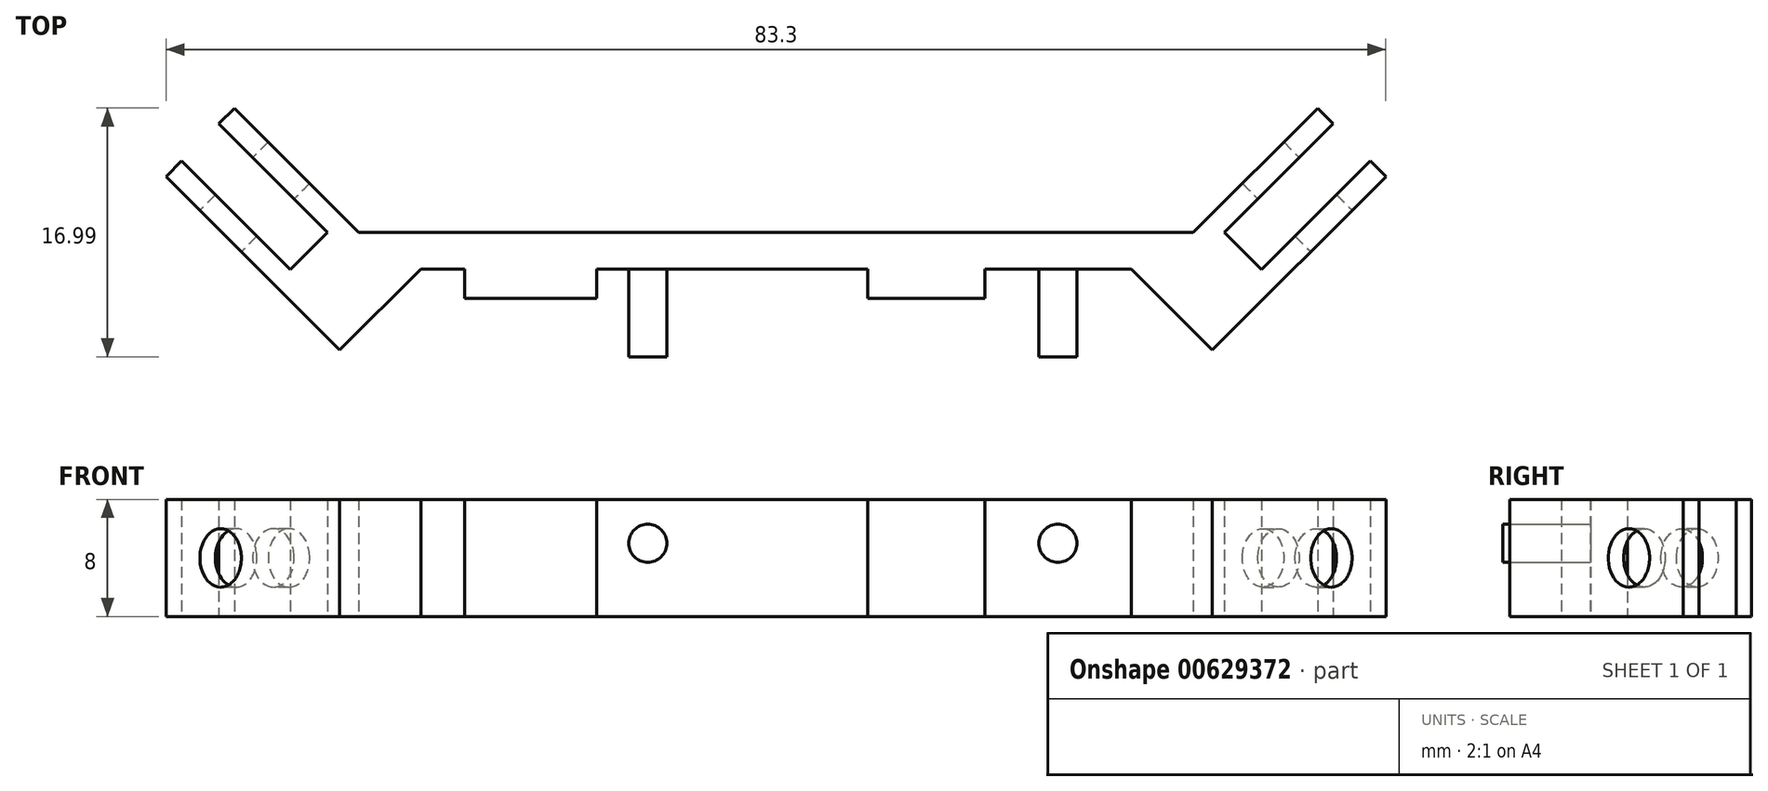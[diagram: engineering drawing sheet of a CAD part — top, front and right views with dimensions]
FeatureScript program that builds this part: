
annotation { "Feature Type Name" : "Feature", "Feature Type Description" : "" }
export const myFeature = defineFeature(function(context is Context, id is Id, definition is map)
    precondition{}
    {
        {
            var Q0;
            Q0=qCreatedBy(makeId("Top.planeOp"),FACE);
            var sketch = newSketch(context, id + "F0", { "sketchPlane" : qUnion([Q0])});
            skLineSegment(sketch, "E0.bottom", {"start": v(-28.5, -30) * mm, "end": v(28.5, -30) * mm});
            skPoint(sketch, "E0.middle", {"position": v(0, 0) * mm});
            skLineSegment(sketch, "E1", {"start": v(30.62, -30) * mm, "end": v(38.05, -22.58) * mm});
            skLineSegment(sketch, "E2.0", {"start": v(33.17, -32.55) * mm, "end": v(40.6, -25.12) * mm});
            skLineSegment(sketch, "E3.0", {"start": v(28.5, -30) * mm, "end": v(36.99, -21.51) * mm});
            skLineSegment(sketch, "E4", {"start": v(30.62, -30) * mm, "end": v(33.17, -32.55) * mm});
            skLineSegment(sketch, "E5.0", {"start": v(29.8, -38.04) * mm, "end": v(41.65, -26.18) * mm});
            skLineSegment(sketch, "E6", {"start": v(36.99, -21.51) * mm, "end": v(38.05, -22.58) * mm});
            skLineSegment(sketch, "E7.0", {"start": v(-24.26, -32.5) * mm, "end": v(24.26, -32.5) * mm});
            skLineSegment(sketch, "E8", {"start": v(24.26, -32.5) * mm, "end": v(29.8, -38.04) * mm});
            skLineSegment(sketch, "E9.trimOffspring", {"start": v(40.6, -25.12) * mm, "end": v(41.65, -26.18) * mm});
            skLineSegment(sketch, "E10.MirrorCS", {"start": v(-24.26, -32.5) * mm, "end": v(-29.8, -38.04) * mm});
            skLineSegment(sketch, "E11.MirrorCS", {"start": v(-29.8, -38.04) * mm, "end": v(-41.65, -26.18) * mm});
            skLineSegment(sketch, "E12.MirrorCS", {"start": v(-40.6, -25.12) * mm, "end": v(-41.65, -26.18) * mm});
            skLineSegment(sketch, "E13.MirrorCS", {"start": v(-33.17, -32.55) * mm, "end": v(-40.6, -25.12) * mm});
            skLineSegment(sketch, "E14.MirrorCS", {"start": v(-30.62, -30) * mm, "end": v(-33.17, -32.55) * mm});
            skLineSegment(sketch, "E15.MirrorCS", {"start": v(-30.62, -30) * mm, "end": v(-38.05, -22.58) * mm});
            skLineSegment(sketch, "E16.MirrorCS", {"start": v(-36.99, -21.51) * mm, "end": v(-38.05, -22.58) * mm});
            skLineSegment(sketch, "E17.MirrorCS", {"start": v(-28.5, -30) * mm, "end": v(-36.99, -21.51) * mm});
            skSolve(sketch);
        }
        {
            var Q0;
            Q0=makeQuery(id+"F0.imprint","IMPRINT",FACE,{"disambiguationData":[TD([[makeQuery(id+"F0.imprint","IMPRINT",EDGE,{"derivedFrom":sQuery(id+"F0.wireOp",EDGE,"E0.bottom")}),-1.0]])]});
            extrude(context, id + "F1", {"entities" : qUnion([Q0]), "depth" : 8 * mm, "offsetDistance" : 25 * mm});
        }
        {
            var Q0;
            Q0=makeQuery(id+"F1.opExtrude","SWEPT_FACE",FACE,{"disambiguationData":[OSD([sQuery(id+"F0.wireOp",EDGE,"E5.0")])]});
            var sketch = newSketch(context, id + "F2", { "sketchPlane" : qUnion([Q0])});
            skLineSegment(sketch, "E18.0", {"start": v(5.67, 8) * mm, "end": v(5.67, 6) * mm});
            skLineSegment(sketch, "E19.0", {"start": v(-10.83, -5) * mm, "end": v(-10.83, -5) * mm});
            skLineSegment(sketch, "E19.1", {"start": v(-10.83, 13) * mm, "end": v(-10.83, -5) * mm});
            skLineSegment(sketch, "E19.2", {"start": v(-10.83, 13) * mm, "end": v(-10.83, 13) * mm});
            skLineSegment(sketch, "E19.3", {"start": v(-10.83, 13) * mm, "end": v(-10.83, -5) * mm});
            skCircle(sketch, "E20", {"center": v(5.67, 4) * mm, "radius": 2 * mm});
            skLineSegment(sketch, "E21.trimOffspring", {"start": v(5.67, 2) * mm, "end": v(5.67, 0) * mm});
            skSolve(sketch);
        }
        {
            var Q0;
            {var subQ0=sQuery(id+"F2.wireOp",EDGE,"E20");var subQ1=makeQuery(id+"F2.imprint","INTERSECT",VERTEX,{"derivedFrom":[sQuery(id+"F2.wireOp",EDGE,"E18.0"),subQ0]});Q0=makeQuery(id+"F2.imprint","IMPRINT",FACE,{"disambiguationData":[TD([[makeQuery(id+"F2.imprint","IMPRINT",EDGE,{"disambiguationData":[TD([[subQ1,-1.0]])],"derivedFrom":subQ0}),1.0]])]});}
            extrude(context, id + "F3", {"entities" : qUnion([Q0]), "operationType" : NewBodyOperationType.REMOVE, "oppositeDirection" : true, "depth" : 10 * mm, "offsetDistance" : 25 * mm});
        }
        {
            var Q0;
            Q0=makeQuery(id+"F1.opExtrude","SWEPT_FACE",FACE,{"disambiguationData":[OSD([sQuery(id+"F0.wireOp",EDGE,"E11.MirrorCS")])]});
            var sketch = newSketch(context, id + "F4", { "sketchPlane" : qUnion([Q0])});
            skLineSegment(sketch, "E22.0", {"start": v(-5.67, 8) * mm, "end": v(-5.67, 6) * mm});
            skCircle(sketch, "E23", {"center": v(-5.67, 4) * mm, "radius": 2 * mm});
            skLineSegment(sketch, "E24.trimOffspring", {"start": v(-5.67, 2) * mm, "end": v(-5.67, 0) * mm});
            skSolve(sketch);
        }
        {
            var Q0;
            {var subQ0=sQuery(id+"F4.wireOp",EDGE,"E23");var subQ1=makeQuery(id+"F4.imprint","INTERSECT",VERTEX,{"derivedFrom":[sQuery(id+"F4.wireOp",EDGE,"E22.0"),subQ0]});Q0=makeQuery(id+"F4.imprint","IMPRINT",FACE,{"disambiguationData":[TD([[makeQuery(id+"F4.imprint","IMPRINT",EDGE,{"disambiguationData":[TD([[subQ1,-1.0]])],"derivedFrom":subQ0}),1.0]])]});}
            extrude(context, id + "F5", {"entities" : qUnion([Q0]), "operationType" : NewBodyOperationType.REMOVE, "oppositeDirection" : true, "depth" : 9.9 * mm, "offsetDistance" : 25 * mm});
        }
        {
            var Q0;
            Q0=makeQuery(id+"F1.opExtrude","SWEPT_FACE",FACE,{"disambiguationData":[OSD([sQuery(id+"F0.wireOp",EDGE,"E7.0")])]});
            var sketch = newSketch(context, id + "F6", { "sketchPlane" : qUnion([Q0])});
            skCircle(sketch, "E25", {"center": v(19.26, 5) * mm, "radius": 1.3 * mm});
            skLineSegment(sketch, "E26.0", {"start": v(14.26, 8) * mm, "end": v(14.26, 0) * mm});
            skLineSegment(sketch, "E27.0", {"start": v(-29.26, -5) * mm, "end": v(29.26, -5) * mm});
            skLineSegment(sketch, "E27.1", {"start": v(-29.26, 13) * mm, "end": v(-29.26, -5) * mm});
            skLineSegment(sketch, "E27.2", {"start": v(29.26, 13) * mm, "end": v(-29.26, 13) * mm});
            skLineSegment(sketch, "E27.3", {"start": v(29.26, -5) * mm, "end": v(29.26, 13) * mm});
            skLineSegment(sketch, "E28.0", {"start": v(6.26, 8) * mm, "end": v(6.26, 0) * mm});
            skLineSegment(sketch, "E29.0", {"start": v(-21.26, 8) * mm, "end": v(-21.26, 0) * mm});
            skLineSegment(sketch, "E30.0", {"start": v(-12.26, 8) * mm, "end": v(-12.26, 0) * mm});
            skCircle(sketch, "E31", {"center": v(-8.76, 5) * mm, "radius": 1.3 * mm});
            skSolve(sketch);
        }
        {
            var Q0;
            {var subQ0=sQuery(id+"F6.wireOp",EDGE,"E29.0");Q0=makeQuery(id+"F6.imprint","IMPRINT",FACE,{"disambiguationData":[TD([[makeQuery(id+"F6.imprint","IMPRINT",EDGE,{"derivedFrom":subQ0}),1.0]])]});}
            var Q1;
            {var subQ0=sQuery(id+"F6.wireOp",EDGE,"E26.0");Q1=makeQuery(id+"F6.imprint","IMPRINT",FACE,{"disambiguationData":[TD([[makeQuery(id+"F6.imprint","IMPRINT",EDGE,{"derivedFrom":subQ0}),-1.0]])]});}
            extrude(context, id + "F7", {"entities" : qUnion([Q0, Q1]), "operationType" : NewBodyOperationType.ADD, "depth" : 2 * mm, "offsetDistance" : 25 * mm});
        }
        {
            var Q0;
            Q0=makeQuery(id+"F6.imprint","IMPRINT",FACE,{"disambiguationData":[TD([[makeQuery(id+"F6.imprint","IMPRINT",EDGE,{"derivedFrom":sQuery(id+"F6.wireOp",EDGE,"E31")}),1.0]])]});
            var Q1;
            Q1=makeQuery(id+"F6.imprint","IMPRINT",FACE,{"disambiguationData":[TD([[makeQuery(id+"F6.imprint","IMPRINT",EDGE,{"derivedFrom":sQuery(id+"F6.wireOp",EDGE,"E25")}),1.0]])]});
            extrude(context, id + "F8", {"entities" : qUnion([Q0, Q1]), "operationType" : NewBodyOperationType.ADD, "depth" : 6 * mm, "offsetDistance" : 25 * mm});
        }
    });
